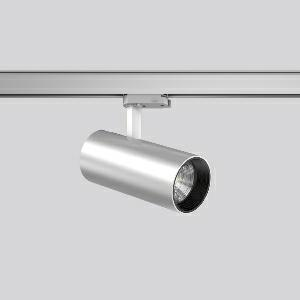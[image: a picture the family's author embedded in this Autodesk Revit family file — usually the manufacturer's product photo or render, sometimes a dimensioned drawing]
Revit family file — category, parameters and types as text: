
# Revit family: deecos_s_mini_742194_004_76_a166
name_source: partatom
category: Lighting Fixtures
units: mm (PartAtom-declared; Revit-internal decimal feet)

## family parameters
Cut with Voids When Loaded = No
Host = Face
Light Source = No
Part Type = Normal
Room Calculation Point = No
Round Connector Dimension = Use Diameter
Shared = No

## types (1)
- DEECOS S mini (1 x LED Modul 930, 2000 lm, 3000)
    Apparent Load = 22 VA
    Approval mark = CE
    CIE Flux Codes = 99 100 100 100 100
    Color Rendering = 90
    Color Temperature = 3000
    Default Elevation = 1800 mm
    Description = Series: DEECOS S mini
LED surface-mounted projector in modern design with no visible cooling ribs. Housing: die-cast aluminium, powder-coated. Rotation range: 356°. Swivel range: 90°. Black plastic ring and recessed LED to prevent glare from the side. Optical assembly with lens made of plastic (polycarbonate) for the best homogeneous light distribution - can be changed without tools. Best colour rendering index Ra>90. Superspot version with small spot LED. With adapter for RZB 3-circuit DALI tracks. Suitable for Track on ceiling, Wall track. High quality converter without flickering and stroboscopic effect. The following accessories can be mounted without use of tools: interchangeable lenses, decorative glasses, honeycomb louvre, clear and frosted diffusers, white interchangeable plastic ring. 
Colour: silver
Diameter: 87 mm
Height: 214 mm
Lamp: LED
Socket: without socket
Colour temperature: 3000K
Colour rendering index (CRI): 92
System power: 22 W
Rated luminous flux: 2000 lm
Luminous efficiency: 91 lm/W
Control gear: Converter, dimmable, DALI
Protection class: I
Type of protection: IP 20
    Height = 214 mm
    Lamp = 1 x LED Modul 930
    Lamp Light Flux = 2000 lm
    Lamp count = 1
    Length = 87 mm
    Lifetime = 50000 h
    Luminous efficacy = 91 lm/W
    Manufacturer = RZB
    ModVariant = No
    Model = 742194.004.76
    Mounting Place = Ceiling
    Mounting Type = Rail mounted
    Number of Poles = 1
    OnlyDefault = Yes
    Power Factor = 1
    Product Name = DEECOS S mini
    Product group = Track mounted projectors
    ProductGroupID = 301
    Protection Class = Protection class I
    Protection Degree = IP 20
    RLX_Detail_Level = 1
    RLX_Emergency_Light_Flux = 0 lm
    RLX_Emergency_Type = 0
    RLX_Emergency_Type_DB = No
    RlxData = <blob elided: 37461 chars, md5=821cf358>
    Socket = socket
    Standby Power = 0 W
    System Light Flux = 2000 lm
    System Power = 22 W
    Type Comments = Product without accessories
    Type Image = 741930.004.jpg
    URL = http://relux.com
    VarID = ---
    Voltage = 230 V
    Voltage Range = 220-240 V
    Weight = 0.00 kg
    Width = 0 mm  [stored 0 ft]

note: [stored X ft] marks values corroborated as IEEE doubles in the binary element streams (Revit-internal decimal feet)

## geometry (parser evidence)
native form markers: Blend x4, Sweep x14
no freeform markers — native parametric forms only
